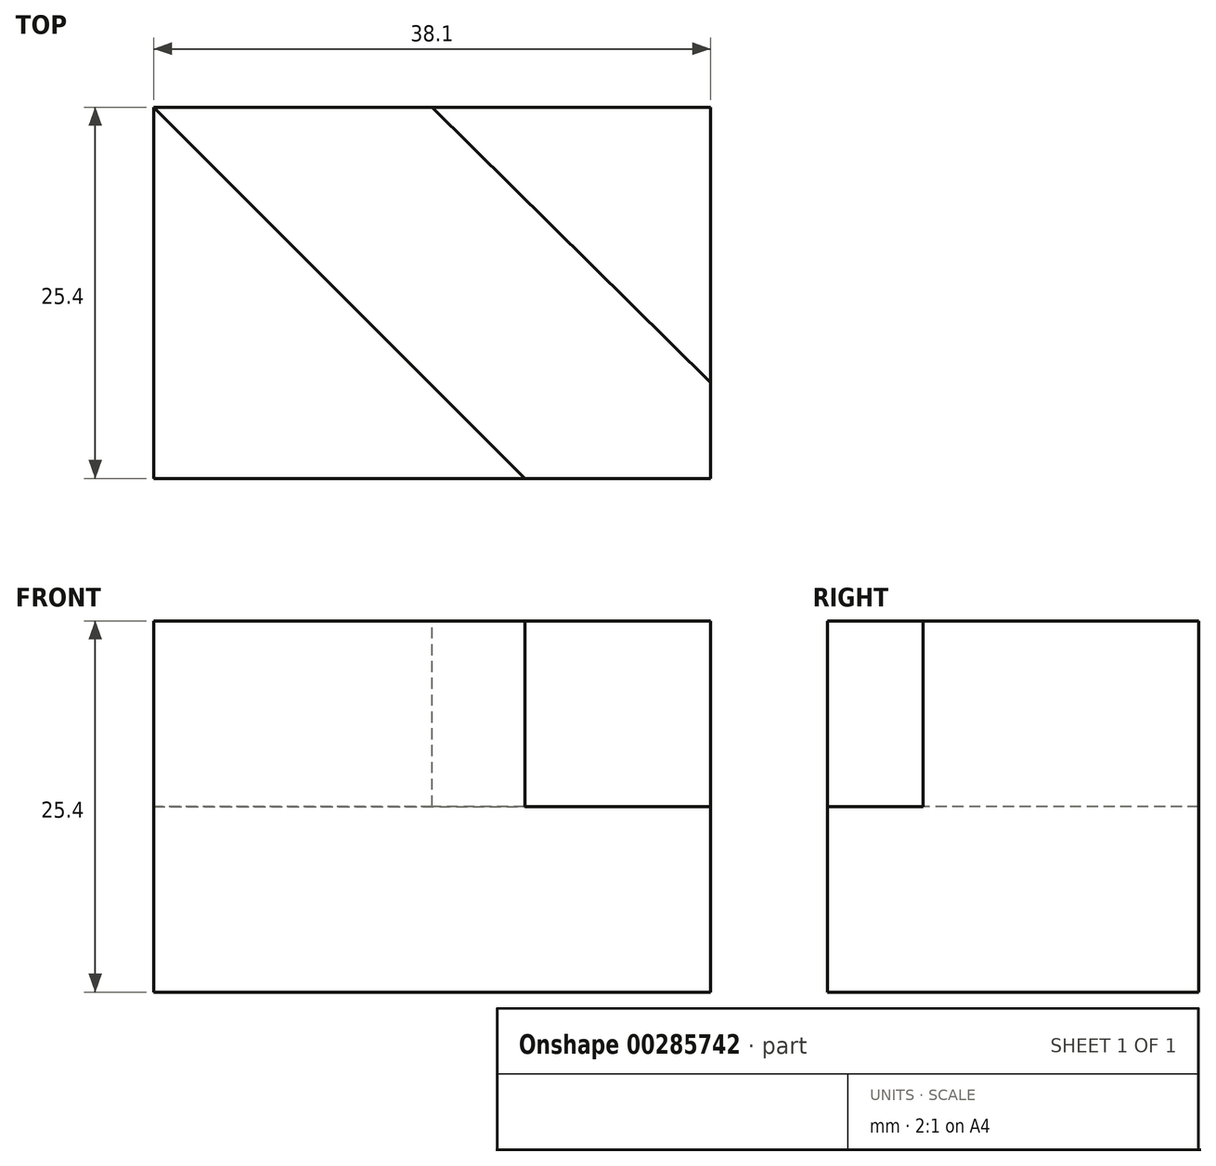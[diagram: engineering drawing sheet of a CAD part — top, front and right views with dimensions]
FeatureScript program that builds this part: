
annotation { "Feature Type Name" : "Feature", "Feature Type Description" : "" }
export const myFeature = defineFeature(function(context is Context, id is Id, definition is map)
    precondition{}
    {
        {
            var Q0;
            Q0=qCreatedBy(makeId("Front.planeOp"),FACE);
            var sketch = newSketch(context, id + "F0", { "sketchPlane" : qUnion([Q0])});
            skLineSegment(sketch, "E0", {"start": v(0, 0) * mm, "end": v(38.1, 0) * mm});
            skLineSegment(sketch, "E1", {"start": v(38.1, 0) * mm, "end": v(38.1, 25.4) * mm});
            skLineSegment(sketch, "E2", {"start": v(38.1, 25.4) * mm, "end": v(0, 25.4) * mm});
            skLineSegment(sketch, "E3", {"start": v(0, 25.4) * mm, "end": v(0, 0) * mm});
            skSolve(sketch);
        }
        {
            var Q0;
            Q0 = qSketchRegion(id + "F0", true);
            extrude(context, id + "F1", {"entities" : qUnion([Q0]), "depth" : 25.4 * mm});
        }
        {
            var Q0;
            Q0=makeQuery(id+"F1.opExtrude","SWEPT_FACE",FACE,{"disambiguationData":[OSD([sQuery(id+"F0.wireOp",EDGE,"E2")])]});
            var sketch = newSketch(context, id + "F2", { "sketchPlane" : qUnion([Q0])});
            skLineSegment(sketch, "E4", {"start": v(38.1, -25.4) * mm, "end": v(25.4, -25.4) * mm});
            skLineSegment(sketch, "E5", {"start": v(25.4, -25.4) * mm, "end": v(38.1, -25.4) * mm});
            skLineSegment(sketch, "E6", {"start": v(0, 0) * mm, "end": v(25.4, -25.4) * mm});
            skLineSegment(sketch, "E7", {"start": v(0, 0) * mm, "end": v(19.05, 0) * mm});
            skLineSegment(sketch, "E8", {"start": v(38.1, -25.4) * mm, "end": v(38.1, -18.84) * mm});
            skLineSegment(sketch, "E9", {"start": v(38.1, -18.84) * mm, "end": v(19.05, 0) * mm});
            skSolve(sketch);
        }
        {
            var Q0;
            Q0 = qSketchRegion(id + "F2", true);
            extrude(context, id + "F3", {"entities" : qUnion([Q0]), "operationType" : NewBodyOperationType.REMOVE, "oppositeDirection" : true, "depth" : 12.7 * mm});
        }
    });
